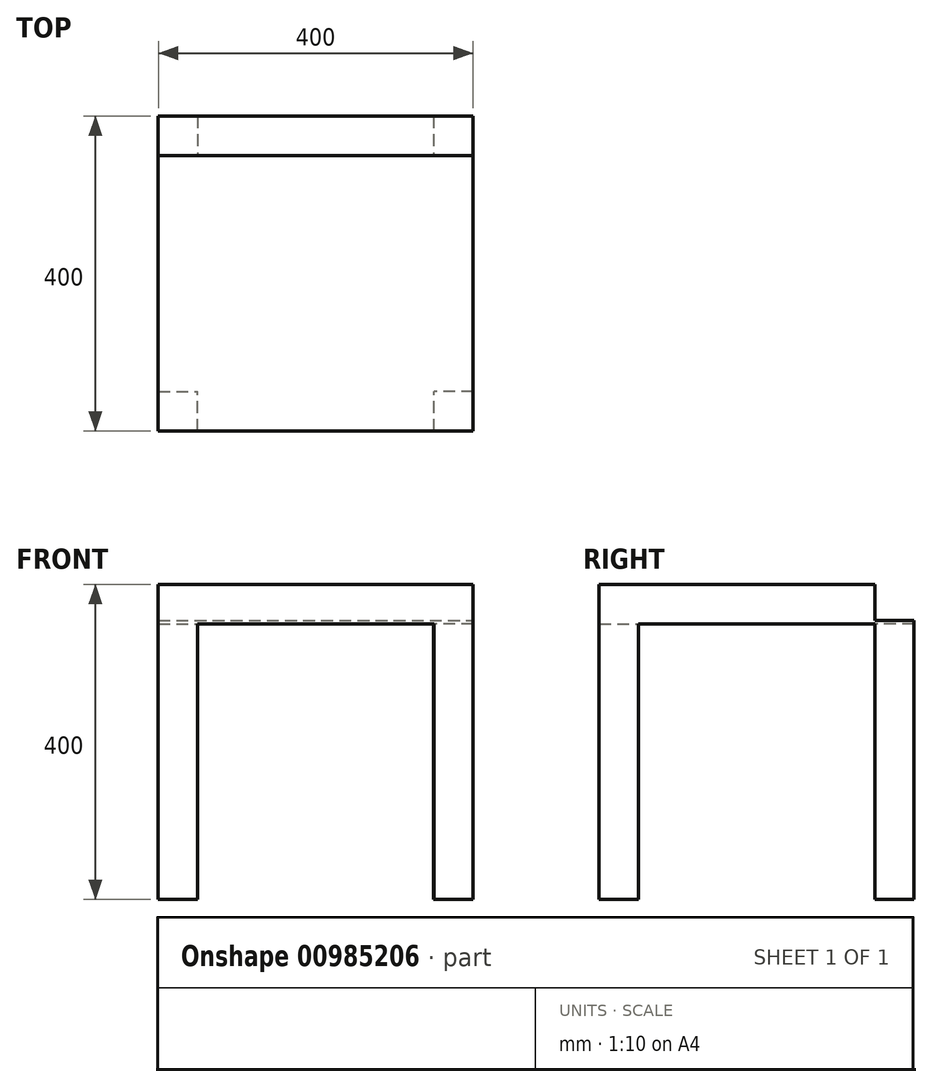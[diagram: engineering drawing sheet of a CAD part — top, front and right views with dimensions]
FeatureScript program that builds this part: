
annotation { "Feature Type Name" : "Feature", "Feature Type Description" : "" }
export const myFeature = defineFeature(function(context is Context, id is Id, definition is map)
    precondition{}
    {
        {
            var Q0;
            Q0=qCreatedBy(makeId("Top.planeOp"),FACE);
            var sketch = newSketch(context, id + "F0", { "sketchPlane" : qUnion([Q0])});
            skLineSegment(sketch, "E0.bottom", {"start": v(-202.55, -156.3) * mm, "end": v(197.45, -156.3) * mm});
            skLineSegment(sketch, "E0.top", {"start": v(-202.55, 243.7) * mm, "end": v(197.45, 243.7) * mm});
            skLineSegment(sketch, "E0.left", {"start": v(-202.55, -156.3) * mm, "end": v(-202.55, 243.7) * mm});
            skLineSegment(sketch, "E0.right", {"start": v(197.45, -156.3) * mm, "end": v(197.45, 243.7) * mm});
            skPoint(sketch, "E1.firstSnap0", {"position": v(-2.55, -156.3) * mm});
            skPoint(sketch, "E1.oppositeSnap0", {"position": v(-2.55, -156.3) * mm});
            skLineSegment(sketch, "E1.bottom", {"start": v(-2.55, -239.66) * mm, "end": v(-2.55, -239.66) * mm});
            skLineSegment(sketch, "E1.top", {"start": v(-2.55, -256.1) * mm, "end": v(-2.55, -256.1) * mm});
            skLineSegment(sketch, "E1.left", {"start": v(-2.55, -239.66) * mm, "end": v(-2.55, -256.1) * mm});
            skLineSegment(sketch, "E1.right", {"start": v(-2.55, -239.66) * mm, "end": v(-2.55, -256.1) * mm});
            skSolve(sketch);
        }
        {
            var Q0;
            Q0=makeQuery(id+"F0.imprint","IMPRINT",FACE,{"disambiguationData":[TD([[makeQuery(id+"F0.imprint","IMPRINT",EDGE,{"derivedFrom":sQuery(id+"F0.wireOp",EDGE,"E0.bottom")}),1.0]])]});
            extrude(context, id + "F1", {"entities" : qUnion([Q0]), "depth" : 350 * mm, "offsetDistance" : 25.4 * mm});
        }
        {
            var Q0;
            Q0=makeQuery(id+"F1.opExtrude","CAP_FACE",FACE,{"disambiguationData":[OSD([sQuery(id+"F0.wireOp",EDGE,"E0.bottom"),sQuery(id+"F0.wireOp",EDGE,"E0.top"),sQuery(id+"F0.wireOp",EDGE,"E0.left"),sQuery(id+"F0.wireOp",EDGE,"E0.right")])],"isStart":false});
            var sketch = newSketch(context, id + "F2", { "sketchPlane" : qUnion([Q0])});
            skLineSegment(sketch, "E2.bottom", {"start": v(-202.55, 243.7) * mm, "end": v(197.45, 243.7) * mm});
            skLineSegment(sketch, "E2.top", {"start": v(-202.55, 193.7) * mm, "end": v(197.45, 193.7) * mm});
            skLineSegment(sketch, "E2.left", {"start": v(-202.55, 243.7) * mm, "end": v(-202.55, 193.7) * mm});
            skLineSegment(sketch, "E2.right", {"start": v(197.45, 243.7) * mm, "end": v(197.45, 193.7) * mm});
            skSolve(sketch);
        }
        {
            var Q0;
            Q0 = qSketchRegion(id + "F2", true);
            extrude(context, id + "F3", {"entities" : qUnion([Q0]), "operationType" : NewBodyOperationType.ADD, "depth" : 300 * mm, "offsetDistance" : 25.4 * mm});
        }
        {
            var Q0;
            Q0=makeQuery(id+"F1.opExtrude","CAP_FACE",FACE,{"disambiguationData":[OSD([sQuery(id+"F0.wireOp",EDGE,"E0.bottom"),sQuery(id+"F0.wireOp",EDGE,"E0.top"),sQuery(id+"F0.wireOp",EDGE,"E0.left"),sQuery(id+"F0.wireOp",EDGE,"E0.right")])],"isStart":true});
            var sketch = newSketch(context, id + "F4", { "sketchPlane" : qUnion([Q0])});
            skLineSegment(sketch, "E3.bottom", {"start": v(-202.55, 156.3) * mm, "end": v(-152.55, 156.3) * mm});
            skLineSegment(sketch, "E3.top", {"start": v(-202.55, 106.3) * mm, "end": v(-152.55, 106.3) * mm});
            skLineSegment(sketch, "E3.left", {"start": v(-202.55, 156.3) * mm, "end": v(-202.55, 106.3) * mm});
            skLineSegment(sketch, "E3.right", {"start": v(-152.55, 156.3) * mm, "end": v(-152.55, 106.3) * mm});
            skLineSegment(sketch, "E4.bottom", {"start": v(197.45, 156.3) * mm, "end": v(147.45, 156.3) * mm});
            skLineSegment(sketch, "E4.top", {"start": v(197.45, 106.3) * mm, "end": v(147.45, 106.3) * mm});
            skLineSegment(sketch, "E4.left", {"start": v(197.45, 156.3) * mm, "end": v(197.45, 106.3) * mm});
            skLineSegment(sketch, "E4.right", {"start": v(147.45, 156.3) * mm, "end": v(147.45, 106.3) * mm});
            skLineSegment(sketch, "E5.bottom", {"start": v(197.45, -243.7) * mm, "end": v(146.75, -243.7) * mm});
            skLineSegment(sketch, "E5.top", {"start": v(197.45, -193.7) * mm, "end": v(146.75, -193.7) * mm});
            skLineSegment(sketch, "E5.left", {"start": v(197.45, -243.7) * mm, "end": v(197.45, -193.7) * mm});
            skLineSegment(sketch, "E5.right", {"start": v(146.75, -243.7) * mm, "end": v(146.75, -193.7) * mm});
            skLineSegment(sketch, "E6.bottom", {"start": v(-202.55, -243.7) * mm, "end": v(-152.55, -243.7) * mm});
            skLineSegment(sketch, "E6.top", {"start": v(-202.55, -193.7) * mm, "end": v(-152.55, -193.7) * mm});
            skLineSegment(sketch, "E6.left", {"start": v(-202.55, -243.7) * mm, "end": v(-202.55, -193.7) * mm});
            skLineSegment(sketch, "E6.right", {"start": v(-152.55, -243.7) * mm, "end": v(-152.55, -193.7) * mm});
            skSolve(sketch);
        }
        {
            var Q0;
            Q0=makeQuery(id+"F1.opExtrude","CAP_FACE",FACE,{"disambiguationData":[OSD([sQuery(id+"F0.wireOp",EDGE,"E0.bottom"),sQuery(id+"F0.wireOp",EDGE,"E0.top"),sQuery(id+"F0.wireOp",EDGE,"E0.left"),sQuery(id+"F0.wireOp",EDGE,"E0.right")])],"isStart":false});
            extrude(context, id + "F5", {"entities" : qUnion([Q0]), "operationType" : NewBodyOperationType.ADD, "depth" : 50 * mm, "offsetDistance" : 25.4 * mm});
        }
        {
            var Q0;
            Q0=makeQuery(id+"F3.opExtrude","CAP_FACE",FACE,{"disambiguationData":[OSD([sQuery(id+"F2.wireOp",EDGE,"E2.bottom"),sQuery(id+"F2.wireOp",EDGE,"E2.top"),sQuery(id+"F2.wireOp",EDGE,"E2.left"),sQuery(id+"F2.wireOp",EDGE,"E2.right")])],"isStart":false});
            extrude(context, id + "F6", {"entities" : qUnion([Q0]), "operationType" : NewBodyOperationType.ADD, "oppositeDirection" : true, "depth" : 250 * mm, "offsetDistance" : 25.4 * mm});
        }
        {
            var Q0;
            Q0=makeQuery(id+"F3.opExtrude","CAP_FACE",FACE,{"disambiguationData":[OSD([sQuery(id+"F2.wireOp",EDGE,"E2.bottom"),sQuery(id+"F2.wireOp",EDGE,"E2.top"),sQuery(id+"F2.wireOp",EDGE,"E2.left"),sQuery(id+"F2.wireOp",EDGE,"E2.right")])],"isStart":false});
            extrude(context, id + "F7", {"entities" : qUnion([Q0]), "operationType" : NewBodyOperationType.REMOVE, "oppositeDirection" : true, "depth" : 250 * mm, "offsetDistance" : 25.4 * mm});
        }
        {
            var Q0;
            Q0=makeQuery(id+"F7.boolean.opBoolean","MERGE",FACE,{"derivedFrom":[makeQuery(id+"F5.opExtrude","CAP_FACE",FACE,{"disambiguationData":[OSD([sQuery(id+"F0.wireOp",EDGE,"E0.bottom"),sQuery(id+"F0.wireOp",EDGE,"E0.top"),sQuery(id+"F0.wireOp",EDGE,"E0.left"),sQuery(id+"F0.wireOp",EDGE,"E0.right")])],"isStart":false})],"fromTools":[makeQuery(id+"F7.opExtrude","CAP_FACE",FACE,{"disambiguationData":[OSD([sQuery(id+"F2.wireOp",EDGE,"E2.bottom"),sQuery(id+"F2.wireOp",EDGE,"E2.top"),sQuery(id+"F2.wireOp",EDGE,"E2.left"),sQuery(id+"F2.wireOp",EDGE,"E2.right")])],"isStart":false})]});
            var sketch = newSketch(context, id + "F8", { "sketchPlane" : qUnion([Q0])});
            skLineSegment(sketch, "E7.bottom", {"start": v(197.45, 243.7) * mm, "end": v(-202.55, 243.7) * mm});
            skLineSegment(sketch, "E7.top", {"start": v(197.45, 340.2) * mm, "end": v(-202.55, 340.2) * mm});
            skLineSegment(sketch, "E7.left", {"start": v(197.45, 243.7) * mm, "end": v(197.45, 340.2) * mm});
            skLineSegment(sketch, "E7.right", {"start": v(-202.55, 243.7) * mm, "end": v(-202.55, 340.2) * mm});
            skSolve(sketch);
        }
        {
            var Q0;
            Q0=makeQuery(id+"F8.imprint","IMPRINT",FACE,{"disambiguationData":[TD([[makeQuery(id+"F8.imprint","IMPRINT",EDGE,{"derivedFrom":sQuery(id+"F8.wireOp",EDGE,"E7.bottom")}),1.0]])]});
            extrude(context, id + "F9", {"entities" : qUnion([Q0]), "operationType" : NewBodyOperationType.ADD, "depth" : 300 * mm, "offsetDistance" : 25.4 * mm});
        }
        {
            var Q0;
            Q0=makeQuery(id+"F9.opExtrude","SWEPT_FACE",FACE,{"disambiguationData":[OSD([sQuery(id+"F8.wireOp",EDGE,"E7.bottom")])]});
            extrude(context, id + "F10", {"entities" : qUnion([Q0]), "operationType" : NewBodyOperationType.ADD, "depth" : 50 * mm, "offsetDistance" : 25.4 * mm});
        }
        {
            var Q0;
            {var subQ5=sQuery(id+"F4.wireOp",EDGE,"E3.top");Q0=makeQuery(id+"F4.imprint","IMPRINT",FACE,{"disambiguationData":[TD([[makeQuery(id+"F4.imprint","IMPRINT",EDGE,{"derivedFrom":subQ5}),-1.0]])]});}
            extrude(context, id + "F11", {"entities" : qUnion([Q0]), "operationType" : NewBodyOperationType.REMOVE, "oppositeDirection" : true, "depth" : 350 * mm, "offsetDistance" : 25.4 * mm});
        }
        {
            var Q0;
            Q0=makeQuery(id+"F9.opExtrude","CAP_FACE",FACE,{"disambiguationData":[OSD([sQuery(id+"F8.wireOp",EDGE,"E7.bottom"),sQuery(id+"F8.wireOp",EDGE,"E7.top"),sQuery(id+"F8.wireOp",EDGE,"E7.left"),sQuery(id+"F8.wireOp",EDGE,"E7.right")])],"isStart":false});
            extrude(context, id + "F12", {"entities" : qUnion([Q0]), "operationType" : NewBodyOperationType.REMOVE, "oppositeDirection" : true, "depth" : 345.44 * mm, "offsetDistance" : 25.4 * mm});
        }
        {
            var Q0;
            Q0=makeQuery(id+"F7.boolean.opBoolean","MERGE",FACE,{"derivedFrom":[makeQuery(id+"F5.opExtrude","CAP_FACE",FACE,{"disambiguationData":[OSD([sQuery(id+"F0.wireOp",EDGE,"E0.bottom"),sQuery(id+"F0.wireOp",EDGE,"E0.top"),sQuery(id+"F0.wireOp",EDGE,"E0.left"),sQuery(id+"F0.wireOp",EDGE,"E0.right")])],"isStart":false})],"fromTools":[makeQuery(id+"F7.opExtrude","CAP_FACE",FACE,{"disambiguationData":[OSD([sQuery(id+"F2.wireOp",EDGE,"E2.bottom"),sQuery(id+"F2.wireOp",EDGE,"E2.top"),sQuery(id+"F2.wireOp",EDGE,"E2.left"),sQuery(id+"F2.wireOp",EDGE,"E2.right")])],"isStart":false})]});
            var Q1;
            Q1=makeQuery(id+"F5.opExtrude","CAP_VERTEX",VERTEX,{"disambiguationData":[OSD([sQuery(id+"F0.wireOp",EDGE,"E0.bottom"),sQuery(id+"F0.wireOp",EDGE,"E0.right")])],"isStart":false});
            cPlane(context, id + "F13", {"entities" : qUnion([Q0, Q1]), "cplaneType" : CPlaneType.PLANE_POINT, "offset" : 25.4 * mm, "width" : 152.4 * mm, "height" : 152.4 * mm});
        }
    });
